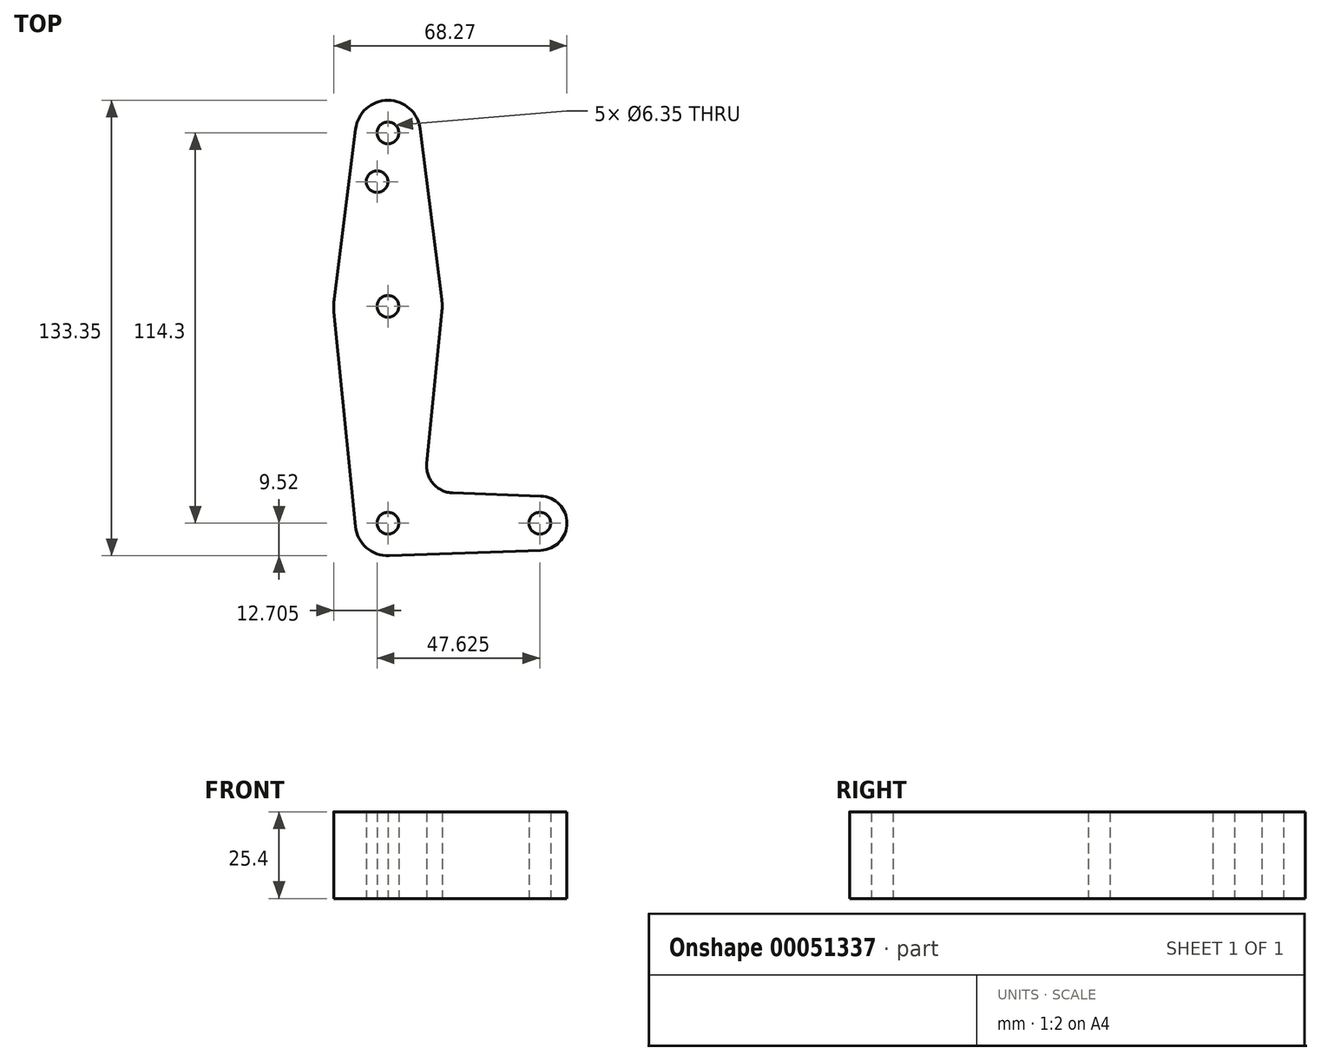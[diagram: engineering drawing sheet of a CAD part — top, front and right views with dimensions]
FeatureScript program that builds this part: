
annotation { "Feature Type Name" : "Feature", "Feature Type Description" : "" }
export const myFeature = defineFeature(function(context is Context, id is Id, definition is map)
    precondition{}
    {
        {
            var Q0;
            Q0=qCreatedBy(makeId("Top.planeOp"),FACE);
            var sketch = newSketch(context, id + "F0", { "sketchPlane" : qUnion([Q0])});
            skLineSegment(sketch, "E0", {"start": v(0, 0) * mm, "end": v(0, 114.3) * mm});
            skLineSegment(sketch, "E1", {"start": v(0, 0) * mm, "end": v(44.45, 0) * mm});
            skCircle(sketch, "E2", {"center": v(0, 114.3) * mm, "radius": 9.53 * mm});
            skCircle(sketch, "E3", {"center": v(0, 63.5) * mm, "radius": 15.88 * mm});
            skCircle(sketch, "E4", {"center": v(0, 0) * mm, "radius": 9.53 * mm});
            skCircle(sketch, "E5", {"center": v(44.45, 0) * mm, "radius": 7.94 * mm});
            skLineSegment(sketch, "E6", {"start": v(9.45, 115.5) * mm, "end": v(15.75, 65.48) * mm});
            skLineSegment(sketch, "E7", {"start": v(-15.75, 65.48) * mm, "end": v(-9.45, 115.5) * mm});
            skLineSegment(sketch, "E8", {"start": v(11.34, 17.6) * mm, "end": v(15.8, 61.91) * mm});
            skLineSegment(sketch, "E9", {"start": v(-9.48, -0.95) * mm, "end": v(-15.8, 61.91) * mm});
            skLineSegment(sketch, "E10", {"start": v(18.97, 8.85) * mm, "end": v(44.73, 7.93) * mm});
            skLineSegment(sketch, "E11", {"start": v(44.73, -7.93) * mm, "end": v(0.34, -9.52) * mm});
            skCircle(sketch, "E12", {"center": v(0, 114.3) * mm, "radius": 3.18 * mm});
            skCircle(sketch, "E13", {"center": v(0, 63.5) * mm, "radius": 3.18 * mm});
            skCircle(sketch, "E14", {"center": v(0, 0) * mm, "radius": 3.18 * mm});
            skCircle(sketch, "E15", {"center": v(44.45, 0) * mm, "radius": 3.18 * mm});
            skCircle(sketch, "E16", {"center": v(-3.18, 100.03) * mm, "radius": 3.18 * mm});
            skArc(sketch, "E17.filletArc", {"start": v(11.34, 17.6) * mm, "mid": v(13.26, 11.57) * mm, "end": v(18.97, 8.85) * mm});
            skSolve(sketch);
        }
        {
            var Q0;
            Q0=makeQuery(id+"F0.imprint","IMPRINT",FACE,{"disambiguationData":[TD([[makeQuery(id+"F0.imprint","IMPRINT",EDGE,{"derivedFrom":sQuery(id+"F0.wireOp",EDGE,"E12")}),-1.0]])]});
            var Q1;
            {var subQ0=sQuery(id+"F0.wireOp",EDGE,"E6");Q1=makeQuery(id+"F0.imprint","IMPRINT",FACE,{"disambiguationData":[TD([[makeQuery(id+"F0.imprint","IMPRINT",EDGE,{"derivedFrom":subQ0}),-1.0]])]});}
            var Q2;
            {var subQ0=sQuery(id+"F0.wireOp",EDGE,"E7");Q2=makeQuery(id+"F0.imprint","IMPRINT",FACE,{"disambiguationData":[TD([[makeQuery(id+"F0.imprint","IMPRINT",EDGE,{"derivedFrom":subQ0}),-1.0]])]});}
            var Q3;
            {var subQ5=sQuery(id+"F0.wireOp",EDGE,"E9");Q3=makeQuery(id+"F0.imprint","IMPRINT",FACE,{"disambiguationData":[TD([[makeQuery(id+"F0.imprint","IMPRINT",EDGE,{"derivedFrom":subQ5}),-1.0]])]});}
            var Q4;
            {var subQ7=sQuery(id+"F0.wireOp",EDGE,"E8");Q4=makeQuery(id+"F0.imprint","IMPRINT",FACE,{"disambiguationData":[TD([[makeQuery(id+"F0.imprint","IMPRINT",EDGE,{"derivedFrom":subQ7}),1.0]])]});}
            var Q5;
            {var subQ0=sQuery(id+"F0.wireOp",EDGE,"E3");var subQ2=sQuery(id+"F0.wireOp",EDGE,"E0");var subQ5=makeQuery(id+"F0.imprint","INTERSECT",VERTEX,{"disambiguationData":[OD(0.0)],"derivedFrom":[subQ2,subQ0]});Q5=makeQuery(id+"F0.imprint","IMPRINT",FACE,{"disambiguationData":[TD([[makeQuery(id+"F0.imprint","IMPRINT",EDGE,{"disambiguationData":[TD([[subQ5,-1.0]])],"derivedFrom":subQ2}),-1.0]])]});}
            var Q6;
            {var subQ0=sQuery(id+"F0.wireOp",EDGE,"E3");var subQ2=sQuery(id+"F0.wireOp",EDGE,"E0");var subQ7=makeQuery(id+"F0.imprint","INTERSECT",VERTEX,{"disambiguationData":[OD(0.0)],"derivedFrom":[subQ2,subQ0]});Q6=makeQuery(id+"F0.imprint","IMPRINT",FACE,{"disambiguationData":[TD([[makeQuery(id+"F0.imprint","IMPRINT",EDGE,{"disambiguationData":[TD([[subQ7,-1.0]])],"derivedFrom":subQ2}),1.0]])]});}
            var Q7;
            {var subQ0=sQuery(id+"F0.wireOp",EDGE,"E14");var subQ1=sQuery(id+"F0.wireOp",EDGE,"E0");var subQ2=makeQuery(id+"F0.imprint","INTERSECT",VERTEX,{"derivedFrom":[subQ1,subQ0]});Q7=makeQuery(id+"F0.imprint","IMPRINT",FACE,{"disambiguationData":[TD([[makeQuery(id+"F0.imprint","IMPRINT",EDGE,{"disambiguationData":[TD([[subQ2,-1.0]])],"derivedFrom":subQ1}),-1.0]])]});}
            var Q8;
            {var subQ3=sQuery(id+"F0.wireOp",EDGE,"E14");var subQ7=sQuery(id+"F0.wireOp",EDGE,"E0");var subQ9=makeQuery(id+"F0.imprint","INTERSECT",VERTEX,{"derivedFrom":[subQ7,subQ3]});Q8=makeQuery(id+"F0.imprint","IMPRINT",FACE,{"disambiguationData":[TD([[makeQuery(id+"F0.imprint","IMPRINT",EDGE,{"disambiguationData":[TD([[subQ9,-1.0]])],"derivedFrom":subQ7}),1.0]])]});}
            var Q9;
            {var subQ5=sQuery(id+"F0.wireOp",EDGE,"E11");Q9=makeQuery(id+"F0.imprint","IMPRINT",FACE,{"disambiguationData":[TD([[makeQuery(id+"F0.imprint","IMPRINT",EDGE,{"derivedFrom":subQ5}),-1.0]])]});}
            var Q10;
            Q10=makeQuery(id+"F0.imprint","IMPRINT",FACE,{"disambiguationData":[TD([[makeQuery(id+"F0.imprint","IMPRINT",EDGE,{"derivedFrom":sQuery(id+"F0.wireOp",EDGE,"E15")}),-1.0]])]});
            extrude(context, id + "F1", {"entities" : qUnion([Q0, Q1, Q2, Q3, Q4, Q5, Q6, Q7, Q8, Q9, Q10]), "depth" : 25.4 * mm});
        }
    });
